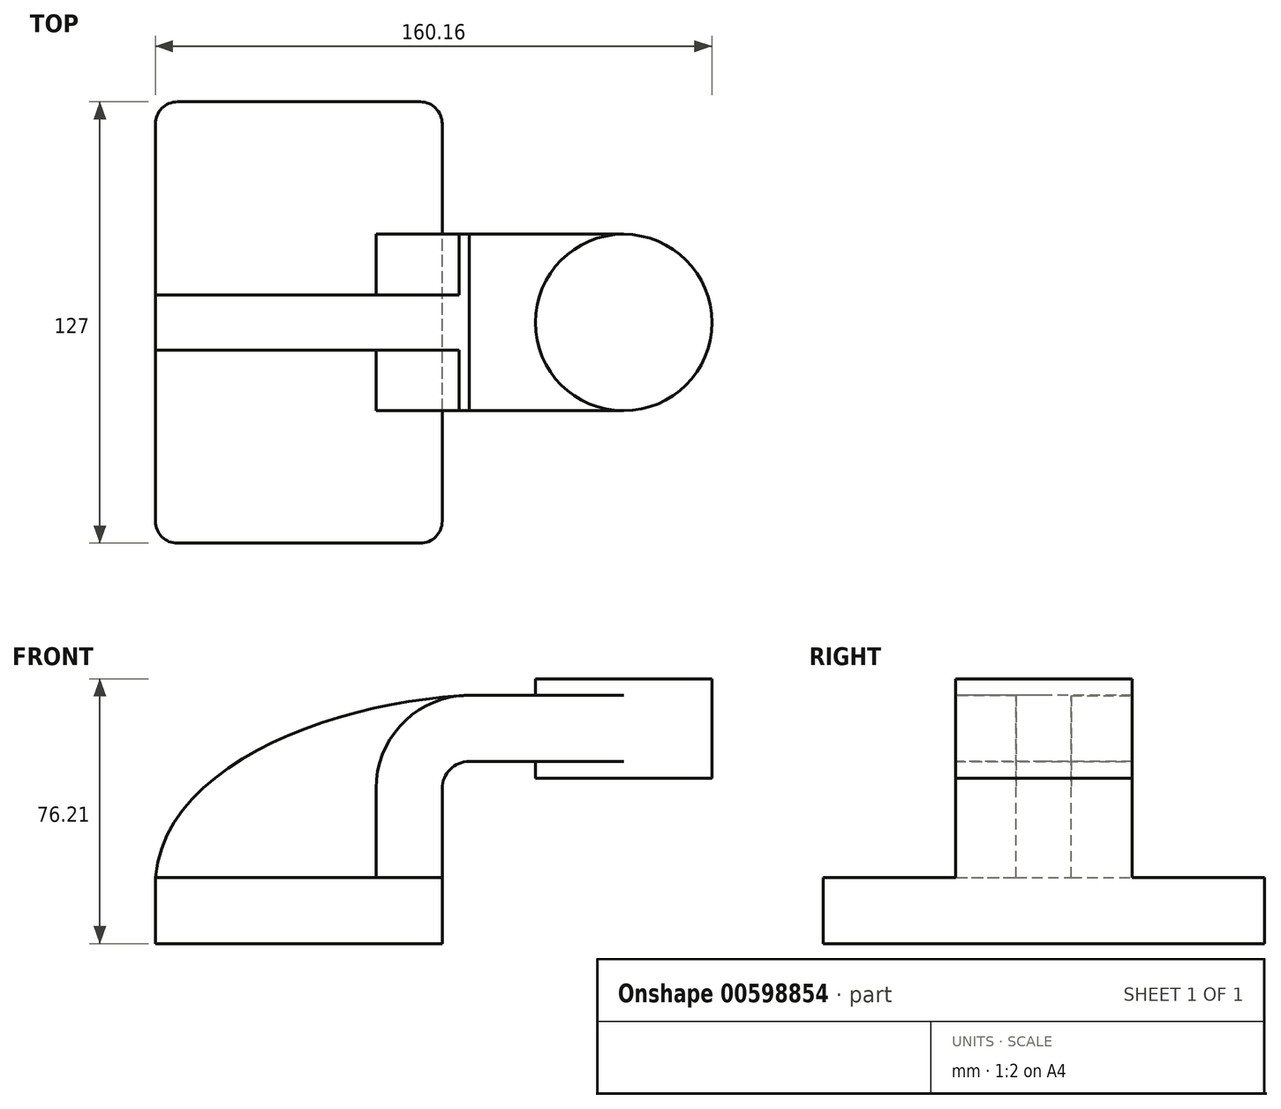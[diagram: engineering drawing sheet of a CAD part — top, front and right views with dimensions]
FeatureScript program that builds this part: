
annotation { "Feature Type Name" : "Feature", "Feature Type Description" : "" }
export const myFeature = defineFeature(function(context is Context, id is Id, definition is map)
    precondition{}
    {
        {
            var Q0;
            Q0=qCreatedBy(makeId("Front.planeOp"),FACE);
            var sketch = newSketch(context, id + "F0", { "sketchPlane" : qUnion([Q0])});
            skLineSegment(sketch, "E0.bottom", {"start": v(-41.27, -9.53) * mm, "end": v(41.28, -9.53) * mm});
            skLineSegment(sketch, "E0.top", {"start": v(-41.28, 9.52) * mm, "end": v(41.28, 9.52) * mm});
            skLineSegment(sketch, "E0.left", {"start": v(-41.28, -9.53) * mm, "end": v(-41.28, 9.52) * mm});
            skLineSegment(sketch, "E0.right", {"start": v(41.28, -9.53) * mm, "end": v(41.28, 9.52) * mm});
            skPoint(sketch, "E0.middle", {"position": v(0, 0) * mm});
            skLineSegment(sketch, "E1.bottom", {"start": v(68.08, 38.1) * mm, "end": v(118.88, 38.1) * mm});
            skLineSegment(sketch, "E1.top", {"start": v(68.08, 66.67) * mm, "end": v(118.88, 66.67) * mm});
            skLineSegment(sketch, "E1.left", {"start": v(68.08, 38.1) * mm, "end": v(68.08, 66.67) * mm});
            skLineSegment(sketch, "E1.right", {"start": v(118.88, 38.1) * mm, "end": v(118.88, 66.67) * mm});
            skPoint(sketch, "E1.middle", {"position": v(93.48, 52.39) * mm});
            skLineSegment(sketch, "E2", {"start": v(41.28, 9.52) * mm, "end": v(41.28, 35.12) * mm});
            skArc(sketch, "E3", {"start": v(41.28, 35.12) * mm, "mid": v(43.55, 40.6) * mm, "end": v(49.03, 42.88) * mm});
            skLineSegment(sketch, "E4", {"start": v(49.03, 42.88) * mm, "end": v(93.48, 42.88) * mm});
            skPoint(sketch, "E4.endSnap0", {"position": v(93.48, 38.1) * mm});
            skLineSegment(sketch, "E5.0", {"start": v(49.03, 61.93) * mm, "end": v(93.48, 61.93) * mm});
            skArc(sketch, "E5.1", {"start": v(22.23, 35.12) * mm, "mid": v(30.08, 54.07) * mm, "end": v(49.03, 61.93) * mm});
            skLineSegment(sketch, "E5.2", {"start": v(22.22, 9.52) * mm, "end": v(22.22, 35.12) * mm});
            skLineSegment(sketch, "E6", {"start": v(93.48, 38.1) * mm, "end": v(93.48, 66.67) * mm});
            skFitSpline(sketch, "E7", {"points": [v(-41.28, 9.53) * mm, v(49.03, 61.93) * mm], "startDerivative": vector(9.1, 101.86) * mm, "endDerivative": vector(107.33, 4.66) * mm});
            skSolve(sketch);
        }
        {
            var Q0;
            Q0=makeQuery(id+"F0.imprint","IMPRINT",FACE,{"disambiguationData":[TD([[makeQuery(id+"F0.imprint","IMPRINT",EDGE,{"derivedFrom":sQuery(id+"F0.wireOp",EDGE,"E0.bottom")}),1.0]])]});
            extrude(context, id + "F1", {"entities" : qUnion([Q0]), "endBound" : BoundingType.SYMMETRIC, "depth" : 127 * mm, "offsetDistance" : 25.4 * mm});
        }
        {
            var Q0;
            {var subQ1=sQuery(id+"F0.wireOp",EDGE,"E2");Q0=makeQuery(id+"F0.imprint","IMPRINT",FACE,{"disambiguationData":[TD([[makeQuery(id+"F0.imprint","IMPRINT",EDGE,{"derivedFrom":subQ1}),1.0]])]});}
            var Q1;
            {var subQ0=sQuery(id+"F0.wireOp",EDGE,"E4");var subQ1=sQuery(id+"F0.wireOp",EDGE,"E1.left");var subQ2=makeQuery(id+"F0.imprint","INTERSECT",VERTEX,{"derivedFrom":[subQ1,subQ0]});Q1=makeQuery(id+"F0.imprint","IMPRINT",FACE,{"disambiguationData":[TD([[makeQuery(id+"F0.imprint","IMPRINT",EDGE,{"disambiguationData":[TD([[subQ2,-1.0]])],"derivedFrom":subQ1}),-1.0]])]});}
            extrude(context, id + "F2", {"entities" : qUnion([Q0, Q1]), "operationType" : NewBodyOperationType.ADD, "endBound" : BoundingType.SYMMETRIC, "depth" : 50.8 * mm, "offsetDistance" : 25.4 * mm});
        }
        {
            var Q0;
            {var subQ3=sQuery(id+"F0.wireOp",EDGE,"E5.2");Q0=makeQuery(id+"F0.imprint","IMPRINT",FACE,{"disambiguationData":[TD([[makeQuery(id+"F0.imprint","IMPRINT",EDGE,{"derivedFrom":subQ3}),1.0]])]});}
            extrude(context, id + "F3", {"entities" : qUnion([Q0]), "operationType" : NewBodyOperationType.ADD, "endBound" : BoundingType.SYMMETRIC, "depth" : 15.88 * mm, "offsetDistance" : 25.4 * mm});
        }
        {
            var Q0;
            {var subQ4=sQuery(id+"F0.wireOp",EDGE,"E1.right");Q0=makeQuery(id+"F0.imprint","IMPRINT",FACE,{"disambiguationData":[TD([[makeQuery(id+"F0.imprint","IMPRINT",EDGE,{"derivedFrom":subQ4}),1.0]])]});}
            var Q1;
            Q1=sQuery(id+"F0.wireOp",EDGE,"E6");
            var Q2;
            Q2=sQuery(id+"F0.wireOp",EDGE,"E6");
            revolve(context, id + "F4", {"operationType" : NewBodyOperationType.ADD, "entities" : qUnion([Q0]), "surfaceEntities" : qUnion([Q1]), "axis" : qUnion([Q2]), "revolveType" : RevolveType.FULL});
        }
        {
            var Q0;
            Q0=makeQuery(id+"F1.opExtrude","CAP_EDGE",EDGE,{"disambiguationData":[OSD([sQuery(id+"F0.wireOp",EDGE,"E0.right")])],"isStart":true});
            var Q1;
            Q1=makeQuery(id+"F1.opExtrude","CAP_EDGE",EDGE,{"disambiguationData":[OSD([sQuery(id+"F0.wireOp",EDGE,"E0.left")])],"isStart":true});
            var Q2;
            Q2=makeQuery(id+"F1.opExtrude","CAP_EDGE",EDGE,{"disambiguationData":[OSD([sQuery(id+"F0.wireOp",EDGE,"E0.right")])],"isStart":false});
            var Q3;
            Q3=makeQuery(id+"F1.opExtrude","CAP_EDGE",EDGE,{"disambiguationData":[OSD([sQuery(id+"F0.wireOp",EDGE,"E0.left")])],"isStart":false});
            fillet(context, id + "F5", {"entities" : qUnion([Q0, Q1, Q2, Q3]), "radius" : 6.35 * mm, "tangentPropagation" : true, "allowEdgeOverflow" : false});
        }
    });
